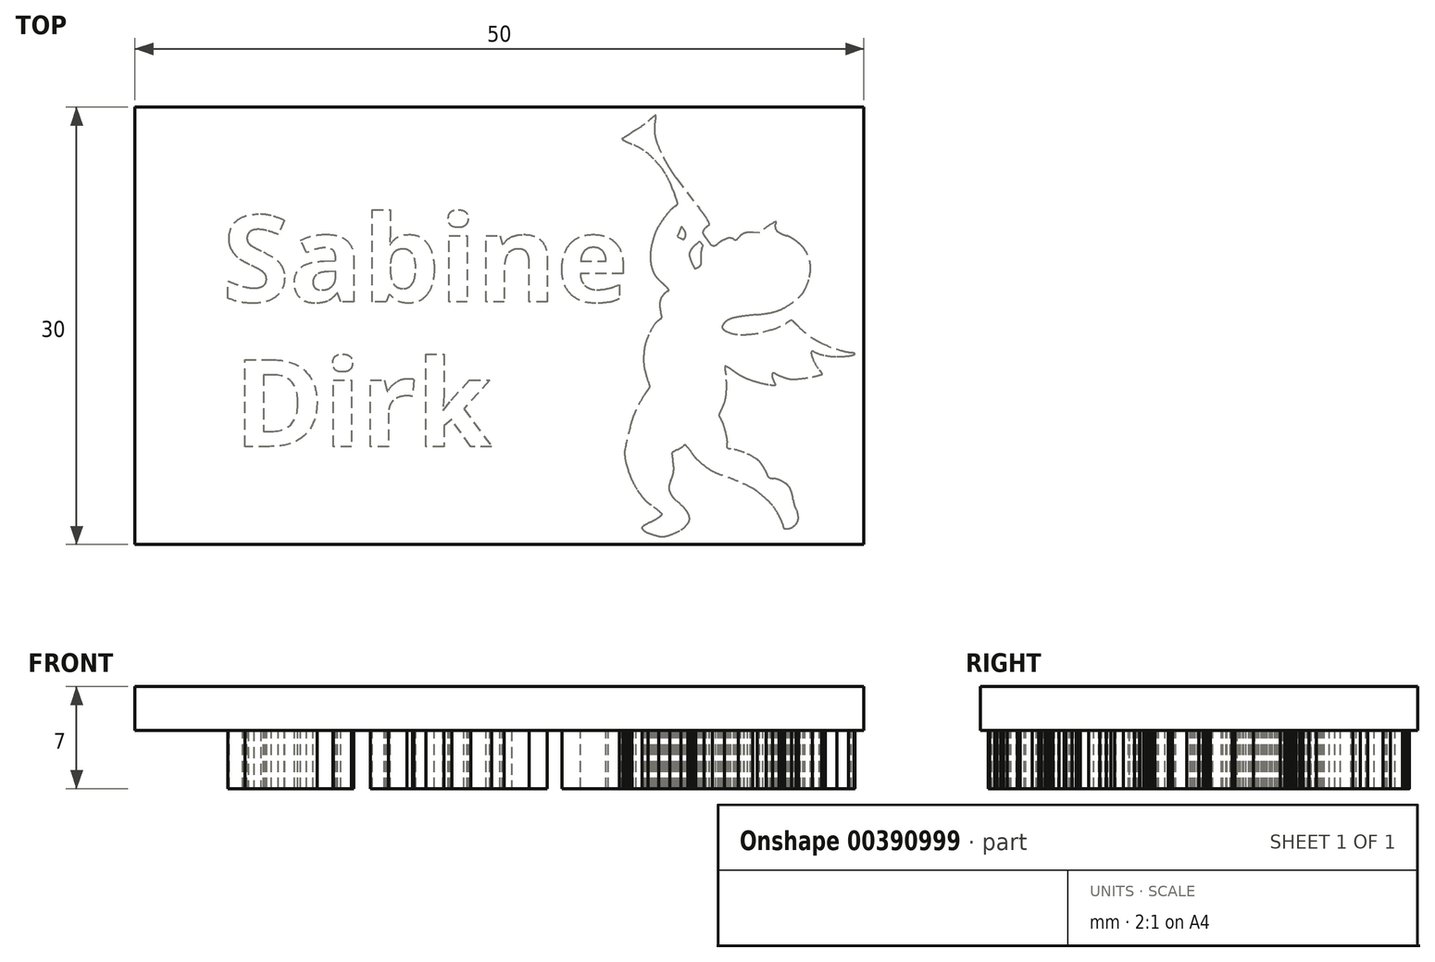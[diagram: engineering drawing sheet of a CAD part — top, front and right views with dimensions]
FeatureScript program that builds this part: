
annotation { "Feature Type Name" : "Feature", "Feature Type Description" : "" }
export const myFeature = defineFeature(function(context is Context, id is Id, definition is map)
    precondition{}
    {
        {
            var Q0;
            Q0=qCreatedBy(makeId("Top.planeOp"),FACE);
            var sketch = newSketch(context, id + "F0", { "sketchPlane" : qUnion([Q0])});
            skLineSegment(sketch, "E0.bottom", {"start": v(25, 15) * mm, "end": v(-25, 15) * mm});
            skLineSegment(sketch, "E0.top", {"start": v(25, -15) * mm, "end": v(-25, -15) * mm});
            skLineSegment(sketch, "E0.left", {"start": v(25, 15) * mm, "end": v(25, -15) * mm});
            skLineSegment(sketch, "E0.right", {"start": v(-25, 15) * mm, "end": v(-25, -15) * mm});
            skPoint(sketch, "E0.middle", {"position": v(0, 0) * mm});
            skSolve(sketch);
        }
        {
            var Q0;
            Q0=makeQuery(id+"F0.imprint","IMPRINT",FACE,{"disambiguationData":[TD([[makeQuery(id+"F0.imprint","IMPRINT",EDGE,{"derivedFrom":sQuery(id+"F0.wireOp",EDGE,"E0.bottom")}),1.0]])]});
            extrude(context, id + "F1", {"entities" : qUnion([Q0]), "depth" : 3 * mm});
        }
        {
            var Q0;
            Q0=makeQuery(id+"F1.opExtrude","CAP_FACE",FACE,{"disambiguationData":[OSD([sQuery(id+"F0.wireOp",EDGE,"E0.bottom"),sQuery(id+"F0.wireOp",EDGE,"E0.top"),sQuery(id+"F0.wireOp",EDGE,"E0.left"),sQuery(id+"F0.wireOp",EDGE,"E0.right")])],"isStart":false});
            var sketch = newSketch(context, id + "F2", { "sketchPlane" : qUnion([Q0])});
            skArc(sketch, "E1", {"start": v(22.16, -3.3) * mm, "mid": v(22.13, -3.26) * mm, "end": v(22.1, -3.21) * mm});
            skArc(sketch, "E2", {"start": v(22.1, -3.21) * mm, "mid": v(22.03, -3.12) * mm, "end": v(21.96, -3.04) * mm});
            skArc(sketch, "E3", {"start": v(21.5, -2.28) * mm, "mid": v(21.7, -2.67) * mm, "end": v(21.96, -3.04) * mm});
            skArc(sketch, "E4", {"start": v(21.43, -2.07) * mm, "mid": v(21.46, -2.18) * mm, "end": v(21.5, -2.28) * mm});
            skArc(sketch, "E5", {"start": v(21.39, -1.87) * mm, "mid": v(21.4, -1.97) * mm, "end": v(21.43, -2.07) * mm});
            skArc(sketch, "E6", {"start": v(21.41, -1.76) * mm, "mid": v(21.4, -1.81) * mm, "end": v(21.39, -1.87) * mm});
            skArc(sketch, "E7", {"start": v(21.46, -1.74) * mm, "mid": v(21.43, -1.75) * mm, "end": v(21.41, -1.76) * mm});
            skArc(sketch, "E8", {"start": v(21.56, -1.77) * mm, "mid": v(21.51, -1.75) * mm, "end": v(21.46, -1.74) * mm});
            skArc(sketch, "E9", {"start": v(21.56, -1.77) * mm, "mid": v(21.95, -1.93) * mm, "end": v(22.36, -2.03) * mm});
            skArc(sketch, "E10", {"start": v(22.36, -2.03) * mm, "mid": v(22.76, -2.1) * mm, "end": v(23.16, -2.12) * mm});
            skArc(sketch, "E11", {"start": v(23.16, -2.12) * mm, "mid": v(23.56, -2.1) * mm, "end": v(23.95, -2.06) * mm});
            skArc(sketch, "E12", {"start": v(23.95, -2.06) * mm, "mid": v(24.14, -2.03) * mm, "end": v(24.32, -1.98) * mm});
            skArc(sketch, "E13", {"start": v(24.32, -1.98) * mm, "mid": v(24.34, -1.97) * mm, "end": v(24.36, -1.96) * mm});
            skArc(sketch, "E14", {"start": v(24.36, -1.96) * mm, "mid": v(24.38, -1.94) * mm, "end": v(24.39, -1.92) * mm});
            skArc(sketch, "E15", {"start": v(24.39, -1.92) * mm, "mid": v(24.36, -1.89) * mm, "end": v(24.31, -1.87) * mm});
            skArc(sketch, "E16", {"start": v(24.31, -1.87) * mm, "mid": v(24.22, -1.85) * mm, "end": v(24.13, -1.84) * mm});
            skArc(sketch, "E17", {"start": v(23.4, -1.68) * mm, "mid": v(23.77, -1.77) * mm, "end": v(24.13, -1.84) * mm});
            skArc(sketch, "E18", {"start": v(22.07, -1.17) * mm, "mid": v(22.72, -1.46) * mm, "end": v(23.4, -1.68) * mm});
            skArc(sketch, "E19", {"start": v(21.48, -0.85) * mm, "mid": v(21.77, -1.02) * mm, "end": v(22.07, -1.17) * mm});
            skArc(sketch, "E20", {"start": v(20.48, -0.01) * mm, "mid": v(20.95, -0.46) * mm, "end": v(21.48, -0.85) * mm});
            skArc(sketch, "E21", {"start": v(20.48, -0.01) * mm, "mid": v(20.37, 0.1) * mm, "end": v(20.26, 0.2) * mm});
            skArc(sketch, "E22", {"start": v(20.26, 0.2) * mm, "mid": v(20.2, 0.25) * mm, "end": v(20.15, 0.3) * mm});
            skLineSegment(sketch, "E23", {"start": v(20.15, 0.3) * mm, "end": v(20.1, 0.35) * mm});
            skArc(sketch, "E24", {"start": v(20.1, 0.35) * mm, "mid": v(20.08, 0.36) * mm, "end": v(20.06, 0.37) * mm});
            skArc(sketch, "E25", {"start": v(20.06, 0.37) * mm, "mid": v(20.05, 0.38) * mm, "end": v(20.03, 0.38) * mm});
            skArc(sketch, "E26", {"start": v(20.03, 0.38) * mm, "mid": v(19.96, 0.35) * mm, "end": v(19.9, 0.31) * mm});
            skArc(sketch, "E27", {"start": v(19.9, 0.31) * mm, "mid": v(19.77, 0.24) * mm, "end": v(19.65, 0.16) * mm});
            skArc(sketch, "E28", {"start": v(18.59, -0.3) * mm, "mid": v(19.13, -0.1) * mm, "end": v(19.65, 0.16) * mm});
            skLineSegment(sketch, "E29", {"start": v(18.59, -0.3) * mm, "end": v(18.07, -0.45) * mm});
            skArc(sketch, "E30", {"start": v(17.03, -0.6) * mm, "mid": v(17.55, -0.54) * mm, "end": v(18.07, -0.45) * mm});
            skArc(sketch, "E31", {"start": v(16.54, -0.6) * mm, "mid": v(16.78, -0.6) * mm, "end": v(17.03, -0.6) * mm});
            skArc(sketch, "E32", {"start": v(15.61, -0.4) * mm, "mid": v(16.06, -0.55) * mm, "end": v(16.54, -0.6) * mm});
            skArc(sketch, "E33", {"start": v(15.42, -0.28) * mm, "mid": v(15.51, -0.34) * mm, "end": v(15.61, -0.4) * mm});
            skArc(sketch, "E34", {"start": v(15.29, -0.11) * mm, "mid": v(15.34, -0.21) * mm, "end": v(15.42, -0.28) * mm});
            skArc(sketch, "E35", {"start": v(15.3, 0) * mm, "mid": v(15.28, -0.06) * mm, "end": v(15.29, -0.11) * mm});
            skArc(sketch, "E36", {"start": v(15.41, 0.17) * mm, "mid": v(15.35, 0.09) * mm, "end": v(15.3, 0) * mm});
            skArc(sketch, "E37", {"start": v(15.75, 0.43) * mm, "mid": v(15.57, 0.32) * mm, "end": v(15.41, 0.17) * mm});
            skArc(sketch, "E38", {"start": v(16.13, 0.56) * mm, "mid": v(15.94, 0.5) * mm, "end": v(15.75, 0.43) * mm});
            skArc(sketch, "E39", {"start": v(16.92, 0.68) * mm, "mid": v(16.52, 0.63) * mm, "end": v(16.13, 0.56) * mm});
            skArc(sketch, "E40", {"start": v(17.66, 0.76) * mm, "mid": v(17.29, 0.72) * mm, "end": v(16.92, 0.68) * mm});
            skArc(sketch, "E41", {"start": v(17.66, 0.76) * mm, "mid": v(18, 0.8) * mm, "end": v(18.35, 0.85) * mm});
            skArc(sketch, "E42", {"start": v(18.35, 0.85) * mm, "mid": v(18.67, 0.91) * mm, "end": v(18.99, 1) * mm});
            skArc(sketch, "E43", {"start": v(18.99, 1) * mm, "mid": v(19.27, 1.1) * mm, "end": v(19.55, 1.24) * mm});
            skArc(sketch, "E44", {"start": v(19.55, 1.24) * mm, "mid": v(20.04, 1.54) * mm, "end": v(20.49, 1.9) * mm});
            skArc(sketch, "E45", {"start": v(20.49, 1.9) * mm, "mid": v(20.67, 2.07) * mm, "end": v(20.83, 2.27) * mm});
            skArc(sketch, "E46", {"start": v(20.83, 2.27) * mm, "mid": v(20.9, 2.36) * mm, "end": v(20.95, 2.47) * mm});
            skArc(sketch, "E47", {"start": v(20.95, 2.47) * mm, "mid": v(21.13, 2.89) * mm, "end": v(21.26, 3.32) * mm});
            skArc(sketch, "E48", {"start": v(21.26, 3.32) * mm, "mid": v(21.3, 3.52) * mm, "end": v(21.34, 3.72) * mm});
            skArc(sketch, "E49", {"start": v(21.34, 3.72) * mm, "mid": v(21.29, 4.46) * mm, "end": v(21, 5.15) * mm});
            skArc(sketch, "E50", {"start": v(21, 5.15) * mm, "mid": v(20.83, 5.38) * mm, "end": v(20.64, 5.58) * mm});
            skArc(sketch, "E51", {"start": v(20.64, 5.58) * mm, "mid": v(20.45, 5.74) * mm, "end": v(20.26, 5.89) * mm});
            skArc(sketch, "E52", {"start": v(20.26, 5.89) * mm, "mid": v(20.08, 6) * mm, "end": v(19.89, 6.11) * mm});
            skArc(sketch, "E53", {"start": v(19.89, 6.11) * mm, "mid": v(19.8, 6.15) * mm, "end": v(19.71, 6.18) * mm});
            skArc(sketch, "E54", {"start": v(19.38, 6.3) * mm, "mid": v(19.55, 6.24) * mm, "end": v(19.71, 6.18) * mm});
            skArc(sketch, "E55", {"start": v(19.11, 6.45) * mm, "mid": v(19.25, 6.37) * mm, "end": v(19.38, 6.3) * mm});
            skArc(sketch, "E56", {"start": v(18.95, 6.66) * mm, "mid": v(19.01, 6.54) * mm, "end": v(19.11, 6.45) * mm});
            skArc(sketch, "E57", {"start": v(18.91, 6.9) * mm, "mid": v(18.92, 6.77) * mm, "end": v(18.95, 6.66) * mm});
            skArc(sketch, "E58", {"start": v(18.94, 6.99) * mm, "mid": v(18.92, 6.94) * mm, "end": v(18.91, 6.9) * mm});
            skArc(sketch, "E59", {"start": v(18.98, 7.02) * mm, "mid": v(18.96, 7) * mm, "end": v(18.94, 6.99) * mm});
            skArc(sketch, "E60", {"start": v(18.98, 7.02) * mm, "mid": v(19, 7.06) * mm, "end": v(19, 7.1) * mm});
            skArc(sketch, "E61", {"start": v(19, 7.1) * mm, "mid": v(18.96, 7.13) * mm, "end": v(18.92, 7.12) * mm});
            skArc(sketch, "E62", {"start": v(18.92, 7.12) * mm, "mid": v(18.84, 7.1) * mm, "end": v(18.77, 7.05) * mm});
            skArc(sketch, "E63", {"start": v(18.77, 7.05) * mm, "mid": v(18.28, 6.74) * mm, "end": v(17.84, 6.36) * mm});
            skLineSegment(sketch, "E64", {"start": v(17.84, 6.36) * mm, "end": v(17.4, 6.4) * mm});
            skArc(sketch, "E65", {"start": v(17.4, 6.4) * mm, "mid": v(17.31, 6.4) * mm, "end": v(17.22, 6.4) * mm});
            skArc(sketch, "E66", {"start": v(17.22, 6.4) * mm, "mid": v(17, 6.4) * mm, "end": v(16.77, 6.34) * mm});
            skArc(sketch, "E67", {"start": v(16.77, 6.34) * mm, "mid": v(16.6, 6.23) * mm, "end": v(16.45, 6.1) * mm});
            skArc(sketch, "E68", {"start": v(16.34, 5.97) * mm, "mid": v(16.4, 6.03) * mm, "end": v(16.45, 6.1) * mm});
            skArc(sketch, "E69", {"start": v(16.21, 5.9) * mm, "mid": v(16.28, 5.92) * mm, "end": v(16.34, 5.97) * mm});
            skArc(sketch, "E70", {"start": v(16.06, 5.95) * mm, "mid": v(16.13, 5.92) * mm, "end": v(16.21, 5.9) * mm});
            skArc(sketch, "E71", {"start": v(16.06, 5.95) * mm, "mid": v(15.93, 6) * mm, "end": v(15.8, 6.03) * mm});
            skArc(sketch, "E72", {"start": v(15.8, 6.03) * mm, "mid": v(15.71, 6.01) * mm, "end": v(15.63, 5.99) * mm});
            skArc(sketch, "E73", {"start": v(15.63, 5.99) * mm, "mid": v(15.46, 5.92) * mm, "end": v(15.29, 5.84) * mm});
            skArc(sketch, "E74", {"start": v(15.29, 5.84) * mm, "mid": v(15.14, 5.75) * mm, "end": v(15, 5.66) * mm});
            skArc(sketch, "E75", {"start": v(14.82, 5.53) * mm, "mid": v(14.92, 5.58) * mm, "end": v(15, 5.66) * mm});
            skArc(sketch, "E76", {"start": v(14.57, 5.52) * mm, "mid": v(14.7, 5.5) * mm, "end": v(14.82, 5.53) * mm});
            skArc(sketch, "E77", {"start": v(14.38, 5.74) * mm, "mid": v(14.46, 5.62) * mm, "end": v(14.57, 5.52) * mm});
            skArc(sketch, "E78", {"start": v(14.38, 5.74) * mm, "mid": v(14.26, 5.92) * mm, "end": v(14.13, 6.1) * mm});
            skArc(sketch, "E79", {"start": v(14, 6.28) * mm, "mid": v(14.05, 6.18) * mm, "end": v(14.13, 6.1) * mm});
            skArc(sketch, "E80", {"start": v(13.98, 6.52) * mm, "mid": v(13.96, 6.4) * mm, "end": v(14, 6.28) * mm});
            skArc(sketch, "E81", {"start": v(14.2, 6.78) * mm, "mid": v(14.07, 6.66) * mm, "end": v(13.98, 6.52) * mm});
            skLineSegment(sketch, "E82", {"start": v(14.2, 6.78) * mm, "end": v(14.42, 6.98) * mm});
            skArc(sketch, "E83", {"start": v(14.42, 6.98) * mm, "mid": v(14.27, 7.27) * mm, "end": v(14.1, 7.55) * mm});
            skArc(sketch, "E84", {"start": v(14.1, 7.55) * mm, "mid": v(13.9, 7.8) * mm, "end": v(13.71, 8.06) * mm});
            skArc(sketch, "E85", {"start": v(12.17, 10.08) * mm, "mid": v(12.93, 9.06) * mm, "end": v(13.71, 8.06) * mm});
            skArc(sketch, "E86", {"start": v(11.83, 10.56) * mm, "mid": v(12, 10.32) * mm, "end": v(12.17, 10.08) * mm});
            skArc(sketch, "E87", {"start": v(11.52, 11.06) * mm, "mid": v(11.67, 10.8) * mm, "end": v(11.83, 10.56) * mm});
            skArc(sketch, "E88", {"start": v(11.52, 11.06) * mm, "mid": v(11.4, 11.32) * mm, "end": v(11.26, 11.57) * mm});
            skArc(sketch, "E89", {"start": v(10.8, 12.6) * mm, "mid": v(11, 12.08) * mm, "end": v(11.26, 11.57) * mm});
            skArc(sketch, "E90", {"start": v(10.66, 13.14) * mm, "mid": v(10.71, 12.87) * mm, "end": v(10.8, 12.6) * mm});
            skArc(sketch, "E91", {"start": v(10.64, 13.68) * mm, "mid": v(10.64, 13.4) * mm, "end": v(10.66, 13.14) * mm});
            skArc(sketch, "E92", {"start": v(10.66, 13.94) * mm, "mid": v(10.65, 13.81) * mm, "end": v(10.64, 13.68) * mm});
            skArc(sketch, "E93", {"start": v(10.69, 14.07) * mm, "mid": v(10.67, 14) * mm, "end": v(10.66, 13.94) * mm});
            skLineSegment(sketch, "E94", {"start": v(10.69, 14.07) * mm, "end": v(10.73, 14.2) * mm});
            skArc(sketch, "E95", {"start": v(10.73, 14.2) * mm, "mid": v(10.74, 14.26) * mm, "end": v(10.75, 14.33) * mm});
            skArc(sketch, "E96", {"start": v(10.75, 14.33) * mm, "mid": v(10.75, 14.36) * mm, "end": v(10.75, 14.4) * mm});
            skArc(sketch, "E97", {"start": v(10.75, 14.4) * mm, "mid": v(10.74, 14.42) * mm, "end": v(10.7, 14.43) * mm});
            skArc(sketch, "E98", {"start": v(10.7, 14.43) * mm, "mid": v(10.65, 14.4) * mm, "end": v(10.6, 14.37) * mm});
            skArc(sketch, "E99", {"start": v(10.6, 14.37) * mm, "mid": v(10.4, 14.2) * mm, "end": v(10.2, 14.04) * mm});
            skArc(sketch, "E100", {"start": v(9.37, 13.45) * mm, "mid": v(9.8, 13.73) * mm, "end": v(10.2, 14.04) * mm});
            skArc(sketch, "E101", {"start": v(9.37, 13.45) * mm, "mid": v(9.16, 13.31) * mm, "end": v(8.96, 13.18) * mm});
            skArc(sketch, "E102", {"start": v(8.54, 12.92) * mm, "mid": v(8.75, 13.04) * mm, "end": v(8.96, 13.18) * mm});
            skArc(sketch, "E103", {"start": v(8.44, 12.86) * mm, "mid": v(8.5, 12.89) * mm, "end": v(8.54, 12.92) * mm});
            skArc(sketch, "E104", {"start": v(8.44, 12.86) * mm, "mid": v(8.42, 12.85) * mm, "end": v(8.41, 12.82) * mm});
            skArc(sketch, "E105", {"start": v(8.41, 12.82) * mm, "mid": v(8.43, 12.8) * mm, "end": v(8.45, 12.77) * mm});
            skArc(sketch, "E106", {"start": v(8.45, 12.77) * mm, "mid": v(8.55, 12.71) * mm, "end": v(8.66, 12.66) * mm});
            skArc(sketch, "E107", {"start": v(8.66, 12.66) * mm, "mid": v(8.87, 12.56) * mm, "end": v(9.09, 12.46) * mm});
            skArc(sketch, "E108", {"start": v(9.9, 12.03) * mm, "mid": v(9.5, 12.26) * mm, "end": v(9.09, 12.46) * mm});
            skArc(sketch, "E109", {"start": v(10.58, 11.44) * mm, "mid": v(10.26, 11.75) * mm, "end": v(9.9, 12.03) * mm});
            skArc(sketch, "E110", {"start": v(11.15, 10.78) * mm, "mid": v(10.88, 11.12) * mm, "end": v(10.58, 11.44) * mm});
            skArc(sketch, "E111", {"start": v(11.39, 10.43) * mm, "mid": v(11.28, 10.61) * mm, "end": v(11.15, 10.78) * mm});
            skArc(sketch, "E112", {"start": v(11.77, 9.7) * mm, "mid": v(11.59, 10.07) * mm, "end": v(11.39, 10.43) * mm});
            skArc(sketch, "E113", {"start": v(11.9, 9.32) * mm, "mid": v(11.84, 9.5) * mm, "end": v(11.77, 9.7) * mm});
            skArc(sketch, "E114", {"start": v(11.9, 9.32) * mm, "mid": v(11.97, 9.13) * mm, "end": v(12.05, 8.95) * mm});
            skArc(sketch, "E115", {"start": v(12.19, 8.58) * mm, "mid": v(12.12, 8.77) * mm, "end": v(12.05, 8.95) * mm});
            skArc(sketch, "E116", {"start": v(12.21, 8.5) * mm, "mid": v(12.2, 8.54) * mm, "end": v(12.19, 8.58) * mm});
            skArc(sketch, "E117", {"start": v(12.23, 8.4) * mm, "mid": v(12.23, 8.44) * mm, "end": v(12.21, 8.5) * mm});
            skArc(sketch, "E118", {"start": v(12.22, 8.35) * mm, "mid": v(12.23, 8.37) * mm, "end": v(12.23, 8.4) * mm});
            skArc(sketch, "E119", {"start": v(12.08, 8.22) * mm, "mid": v(12.16, 8.28) * mm, "end": v(12.22, 8.35) * mm});
            skArc(sketch, "E120", {"start": v(12.08, 8.22) * mm, "mid": v(11.93, 8.1) * mm, "end": v(11.8, 7.98) * mm});
            skArc(sketch, "E121", {"start": v(11.8, 7.98) * mm, "mid": v(11.54, 7.7) * mm, "end": v(11.31, 7.42) * mm});
            skArc(sketch, "E122", {"start": v(11.31, 7.42) * mm, "mid": v(11.11, 7.12) * mm, "end": v(10.92, 6.82) * mm});
            skArc(sketch, "E123", {"start": v(10.92, 6.82) * mm, "mid": v(10.75, 6.51) * mm, "end": v(10.63, 6.19) * mm});
            skArc(sketch, "E124", {"start": v(10.63, 6.19) * mm, "mid": v(10.53, 5.87) * mm, "end": v(10.44, 5.54) * mm});
            skArc(sketch, "E125", {"start": v(10.44, 5.54) * mm, "mid": v(10.39, 5.22) * mm, "end": v(10.36, 4.9) * mm});
            skArc(sketch, "E126", {"start": v(10.36, 4.9) * mm, "mid": v(10.36, 4.58) * mm, "end": v(10.4, 4.26) * mm});
            skArc(sketch, "E127", {"start": v(10.4, 4.26) * mm, "mid": v(10.46, 3.96) * mm, "end": v(10.57, 3.68) * mm});
            skArc(sketch, "E128", {"start": v(10.57, 3.68) * mm, "mid": v(10.63, 3.54) * mm, "end": v(10.71, 3.42) * mm});
            skArc(sketch, "E129", {"start": v(10.71, 3.42) * mm, "mid": v(10.9, 3.2) * mm, "end": v(11.1, 3) * mm});
            skArc(sketch, "E130", {"start": v(11.52, 2.6) * mm, "mid": v(11.32, 2.8) * mm, "end": v(11.1, 3) * mm});
            skArc(sketch, "E131", {"start": v(11.6, 2.5) * mm, "mid": v(11.57, 2.55) * mm, "end": v(11.52, 2.6) * mm});
            skArc(sketch, "E132", {"start": v(11.57, 2.38) * mm, "mid": v(11.62, 2.43) * mm, "end": v(11.6, 2.5) * mm});
            skArc(sketch, "E133", {"start": v(11.57, 2.38) * mm, "mid": v(11.5, 2.36) * mm, "end": v(11.45, 2.32) * mm});
            skArc(sketch, "E134", {"start": v(11.45, 2.32) * mm, "mid": v(11.26, 2.14) * mm, "end": v(11.1, 1.92) * mm});
            skArc(sketch, "E135", {"start": v(11.1, 1.92) * mm, "mid": v(11.02, 1.68) * mm, "end": v(11, 1.42) * mm});
            skArc(sketch, "E136", {"start": v(11, 1.42) * mm, "mid": v(11.02, 1.17) * mm, "end": v(11.07, 0.92) * mm});
            skArc(sketch, "E137", {"start": v(11.14, 0.69) * mm, "mid": v(11.1, 0.8) * mm, "end": v(11.07, 0.92) * mm});
            skArc(sketch, "E138", {"start": v(11.15, 0.57) * mm, "mid": v(11.15, 0.63) * mm, "end": v(11.14, 0.69) * mm});
            skArc(sketch, "E139", {"start": v(11.07, 0.48) * mm, "mid": v(11.11, 0.52) * mm, "end": v(11.15, 0.57) * mm});
            skArc(sketch, "E140", {"start": v(11.07, 0.48) * mm, "mid": v(10.98, 0.4) * mm, "end": v(10.88, 0.34) * mm});
            skArc(sketch, "E141", {"start": v(10.88, 0.34) * mm, "mid": v(10.79, 0.27) * mm, "end": v(10.7, 0.18) * mm});
            skArc(sketch, "E142", {"start": v(10.7, 0.18) * mm, "mid": v(10.46, -0.2) * mm, "end": v(10.25, -0.6) * mm});
            skArc(sketch, "E143", {"start": v(10.25, -0.6) * mm, "mid": v(10.13, -0.9) * mm, "end": v(10.02, -1.2) * mm});
            skArc(sketch, "E144", {"start": v(10.02, -1.2) * mm, "mid": v(9.97, -1.4) * mm, "end": v(9.94, -1.6) * mm});
            skArc(sketch, "E145", {"start": v(9.94, -1.6) * mm, "mid": v(9.9, -2) * mm, "end": v(9.9, -2.4) * mm});
            skArc(sketch, "E146", {"start": v(9.9, -2.4) * mm, "mid": v(9.92, -2.76) * mm, "end": v(10, -3.13) * mm});
            skArc(sketch, "E147", {"start": v(10, -3.13) * mm, "mid": v(10.08, -3.46) * mm, "end": v(10.19, -3.8) * mm});
            skLineSegment(sketch, "E148", {"start": v(10.19, -3.8) * mm, "end": v(10.3, -4.1) * mm});
            skArc(sketch, "E149", {"start": v(10.3, -4.25) * mm, "mid": v(10.32, -4.18) * mm, "end": v(10.3, -4.1) * mm});
            skArc(sketch, "E150", {"start": v(10.11, -4.5) * mm, "mid": v(10.21, -4.38) * mm, "end": v(10.3, -4.25) * mm});
            skArc(sketch, "E151", {"start": v(10.11, -4.5) * mm, "mid": v(10.02, -4.62) * mm, "end": v(9.94, -4.75) * mm});
            skArc(sketch, "E152", {"start": v(9.94, -4.75) * mm, "mid": v(9.64, -5.25) * mm, "end": v(9.38, -5.77) * mm});
            skArc(sketch, "E153", {"start": v(9.38, -5.77) * mm, "mid": v(9.27, -6) * mm, "end": v(9.17, -6.24) * mm});
            skArc(sketch, "E154", {"start": v(9.17, -6.24) * mm, "mid": v(9.1, -6.47) * mm, "end": v(9.03, -6.7) * mm});
            skArc(sketch, "E155", {"start": v(9.03, -6.7) * mm, "mid": v(8.81, -7.57) * mm, "end": v(8.61, -8.45) * mm});
            skArc(sketch, "E156", {"start": v(8.61, -8.45) * mm, "mid": v(8.6, -8.61) * mm, "end": v(8.6, -8.78) * mm});
            skArc(sketch, "E157", {"start": v(8.6, -8.78) * mm, "mid": v(8.62, -9.1) * mm, "end": v(8.68, -9.4) * mm});
            skArc(sketch, "E158", {"start": v(8.68, -9.4) * mm, "mid": v(8.72, -9.54) * mm, "end": v(8.76, -9.67) * mm});
            skArc(sketch, "E159", {"start": v(8.76, -9.67) * mm, "mid": v(8.8, -9.8) * mm, "end": v(8.85, -9.91) * mm});
            skArc(sketch, "E160", {"start": v(8.93, -10.15) * mm, "mid": v(8.9, -10.03) * mm, "end": v(8.85, -9.91) * mm});
            skArc(sketch, "E161", {"start": v(8.93, -10.15) * mm, "mid": v(9, -10.36) * mm, "end": v(9.09, -10.57) * mm});
            skArc(sketch, "E162", {"start": v(9.09, -10.57) * mm, "mid": v(9.27, -10.93) * mm, "end": v(9.47, -11.27) * mm});
            skArc(sketch, "E163", {"start": v(9.47, -11.27) * mm, "mid": v(9.64, -11.52) * mm, "end": v(9.82, -11.76) * mm});
            skArc(sketch, "E164", {"start": v(9.82, -11.76) * mm, "mid": v(9.96, -11.92) * mm, "end": v(10.13, -12.08) * mm});
            skArc(sketch, "E165", {"start": v(10.13, -12.08) * mm, "mid": v(10.26, -12.18) * mm, "end": v(10.4, -12.28) * mm});
            skArc(sketch, "E166", {"start": v(11.18, -12.91) * mm, "mid": v(10.8, -12.59) * mm, "end": v(10.4, -12.28) * mm});
            skArc(sketch, "E167", {"start": v(11.01, -13.08) * mm, "mid": v(11.1, -13) * mm, "end": v(11.18, -12.91) * mm});
            skArc(sketch, "E168", {"start": v(10.63, -13.32) * mm, "mid": v(10.83, -13.21) * mm, "end": v(11.01, -13.08) * mm});
            skArc(sketch, "E169", {"start": v(10.29, -13.5) * mm, "mid": v(10.46, -13.41) * mm, "end": v(10.63, -13.32) * mm});
            skArc(sketch, "E170", {"start": v(10.29, -13.5) * mm, "mid": v(10.13, -13.58) * mm, "end": v(9.98, -13.67) * mm});
            skArc(sketch, "E171", {"start": v(9.98, -13.67) * mm, "mid": v(9.92, -13.7) * mm, "end": v(9.86, -13.75) * mm});
            skArc(sketch, "E172", {"start": v(9.86, -13.75) * mm, "mid": v(9.8, -13.8) * mm, "end": v(9.77, -13.86) * mm});
            skArc(sketch, "E173", {"start": v(9.77, -13.86) * mm, "mid": v(9.78, -13.9) * mm, "end": v(9.8, -13.92) * mm});
            skArc(sketch, "E174", {"start": v(9.8, -13.92) * mm, "mid": v(9.97, -14.1) * mm, "end": v(10.2, -14.21) * mm});
            skArc(sketch, "E175", {"start": v(10.2, -14.21) * mm, "mid": v(10.56, -14.33) * mm, "end": v(10.93, -14.43) * mm});
            skArc(sketch, "E176", {"start": v(10.93, -14.43) * mm, "mid": v(11.12, -14.46) * mm, "end": v(11.32, -14.45) * mm});
            skArc(sketch, "E177", {"start": v(11.32, -14.45) * mm, "mid": v(11.5, -14.41) * mm, "end": v(11.69, -14.35) * mm});
            skArc(sketch, "E178", {"start": v(11.69, -14.35) * mm, "mid": v(12.07, -14.2) * mm, "end": v(12.44, -14.01) * mm});
            skArc(sketch, "E179", {"start": v(12.44, -14.01) * mm, "mid": v(12.7, -13.82) * mm, "end": v(12.92, -13.58) * mm});
            skArc(sketch, "E180", {"start": v(12.92, -13.58) * mm, "mid": v(13, -13.43) * mm, "end": v(13.05, -13.26) * mm});
            skArc(sketch, "E181", {"start": v(13.05, -13.26) * mm, "mid": v(13.04, -13.12) * mm, "end": v(13, -13) * mm});
            skArc(sketch, "E182", {"start": v(13, -13) * mm, "mid": v(12.88, -12.75) * mm, "end": v(12.7, -12.54) * mm});
            skArc(sketch, "E183", {"start": v(12.7, -12.54) * mm, "mid": v(12.43, -12.25) * mm, "end": v(12.12, -11.99) * mm});
            skArc(sketch, "E184", {"start": v(11.8, -11.6) * mm, "mid": v(11.94, -11.8) * mm, "end": v(12.12, -11.99) * mm});
            skArc(sketch, "E185", {"start": v(11.62, -11.16) * mm, "mid": v(11.69, -11.4) * mm, "end": v(11.8, -11.6) * mm});
            skArc(sketch, "E186", {"start": v(11.64, -10.95) * mm, "mid": v(11.62, -11.05) * mm, "end": v(11.62, -11.16) * mm});
            skArc(sketch, "E187", {"start": v(11.76, -10.62) * mm, "mid": v(11.7, -10.78) * mm, "end": v(11.64, -10.95) * mm});
            skArc(sketch, "E188", {"start": v(11.76, -10.62) * mm, "mid": v(11.83, -10.44) * mm, "end": v(11.9, -10.27) * mm});
            skArc(sketch, "E189", {"start": v(11.9, -10.27) * mm, "mid": v(11.93, -10.15) * mm, "end": v(11.95, -10.04) * mm});
            skArc(sketch, "E190", {"start": v(11.95, -10.04) * mm, "mid": v(11.97, -9.86) * mm, "end": v(11.96, -9.69) * mm});
            skArc(sketch, "E191", {"start": v(11.96, -9.69) * mm, "mid": v(11.94, -9.47) * mm, "end": v(11.9, -9.25) * mm});
            skArc(sketch, "E192", {"start": v(11.84, -8.9) * mm, "mid": v(11.87, -9.07) * mm, "end": v(11.9, -9.25) * mm});
            skArc(sketch, "E193", {"start": v(11.84, -8.71) * mm, "mid": v(11.83, -8.8) * mm, "end": v(11.84, -8.9) * mm});
            skArc(sketch, "E194", {"start": v(11.96, -8.63) * mm, "mid": v(11.9, -8.67) * mm, "end": v(11.84, -8.71) * mm});
            skArc(sketch, "E195", {"start": v(12.2, -8.5) * mm, "mid": v(12.08, -8.56) * mm, "end": v(11.96, -8.63) * mm});
            skArc(sketch, "E196", {"start": v(12.2, -8.5) * mm, "mid": v(12.33, -8.43) * mm, "end": v(12.46, -8.36) * mm});
            skArc(sketch, "E197", {"start": v(12.46, -8.36) * mm, "mid": v(12.53, -8.3) * mm, "end": v(12.6, -8.25) * mm});
            skArc(sketch, "E198", {"start": v(12.73, -8.17) * mm, "mid": v(12.66, -8.2) * mm, "end": v(12.6, -8.25) * mm});
            skArc(sketch, "E199", {"start": v(12.82, -8.23) * mm, "mid": v(12.78, -8.2) * mm, "end": v(12.73, -8.17) * mm});
            skArc(sketch, "E200", {"start": v(13.26, -8.81) * mm, "mid": v(13.06, -8.5) * mm, "end": v(12.82, -8.23) * mm});
            skArc(sketch, "E201", {"start": v(13.26, -8.81) * mm, "mid": v(13.36, -8.95) * mm, "end": v(13.48, -9.07) * mm});
            skArc(sketch, "E202", {"start": v(13.48, -9.07) * mm, "mid": v(13.75, -9.33) * mm, "end": v(14.04, -9.58) * mm});
            skArc(sketch, "E203", {"start": v(14.04, -9.58) * mm, "mid": v(14.32, -9.78) * mm, "end": v(14.6, -9.97) * mm});
            skArc(sketch, "E204", {"start": v(14.6, -9.97) * mm, "mid": v(15.01, -10.14) * mm, "end": v(15.43, -10.3) * mm});
            skArc(sketch, "E205", {"start": v(16.38, -10.68) * mm, "mid": v(15.9, -10.48) * mm, "end": v(15.43, -10.3) * mm});
            skArc(sketch, "E206", {"start": v(17.38, -11.16) * mm, "mid": v(16.89, -10.91) * mm, "end": v(16.38, -10.68) * mm});
            skArc(sketch, "E207", {"start": v(17.7, -11.37) * mm, "mid": v(17.54, -11.26) * mm, "end": v(17.38, -11.16) * mm});
            skArc(sketch, "E208", {"start": v(18.3, -11.88) * mm, "mid": v(18, -11.62) * mm, "end": v(17.7, -11.37) * mm});
            skArc(sketch, "E209", {"start": v(18.75, -12.34) * mm, "mid": v(18.54, -12.1) * mm, "end": v(18.3, -11.88) * mm});
            skArc(sketch, "E210", {"start": v(19.18, -13.01) * mm, "mid": v(18.97, -12.67) * mm, "end": v(18.75, -12.34) * mm});
            skArc(sketch, "E211", {"start": v(19.41, -13.55) * mm, "mid": v(19.31, -13.28) * mm, "end": v(19.18, -13.01) * mm});
            skArc(sketch, "E212", {"start": v(19.41, -13.55) * mm, "mid": v(19.45, -13.7) * mm, "end": v(19.49, -13.86) * mm});
            skArc(sketch, "E213", {"start": v(19.49, -13.86) * mm, "mid": v(19.52, -13.9) * mm, "end": v(19.56, -13.9) * mm});
            skArc(sketch, "E214", {"start": v(19.56, -13.9) * mm, "mid": v(19.81, -13.91) * mm, "end": v(20.05, -13.85) * mm});
            skArc(sketch, "E215", {"start": v(20.05, -13.85) * mm, "mid": v(20.21, -13.73) * mm, "end": v(20.35, -13.6) * mm});
            skArc(sketch, "E216", {"start": v(20.35, -13.6) * mm, "mid": v(20.42, -13.5) * mm, "end": v(20.48, -13.4) * mm});
            skArc(sketch, "E217", {"start": v(20.48, -13.4) * mm, "mid": v(20.5, -13.3) * mm, "end": v(20.5, -13.18) * mm});
            skArc(sketch, "E218", {"start": v(20.5, -13.18) * mm, "mid": v(20.46, -12.8) * mm, "end": v(20.3, -12.47) * mm});
            skArc(sketch, "E219", {"start": v(20.22, -12.28) * mm, "mid": v(20.25, -12.38) * mm, "end": v(20.3, -12.47) * mm});
            skArc(sketch, "E220", {"start": v(20.16, -11.97) * mm, "mid": v(20.18, -12.12) * mm, "end": v(20.22, -12.28) * mm});
            skArc(sketch, "E221", {"start": v(20.16, -11.97) * mm, "mid": v(20.14, -11.82) * mm, "end": v(20.11, -11.66) * mm});
            skArc(sketch, "E222", {"start": v(20.11, -11.66) * mm, "mid": v(20.09, -11.56) * mm, "end": v(20.06, -11.46) * mm});
            skArc(sketch, "E223", {"start": v(20.06, -11.46) * mm, "mid": v(19.97, -11.21) * mm, "end": v(19.83, -10.99) * mm});
            skArc(sketch, "E224", {"start": v(19.83, -10.99) * mm, "mid": v(19.74, -10.9) * mm, "end": v(19.63, -10.8) * mm});
            skArc(sketch, "E225", {"start": v(19.63, -10.8) * mm, "mid": v(19.42, -10.68) * mm, "end": v(19.2, -10.57) * mm});
            skArc(sketch, "E226", {"start": v(19.2, -10.57) * mm, "mid": v(19, -10.5) * mm, "end": v(18.79, -10.47) * mm});
            skArc(sketch, "E227", {"start": v(18.62, -10.45) * mm, "mid": v(18.7, -10.47) * mm, "end": v(18.79, -10.47) * mm});
            skArc(sketch, "E228", {"start": v(18.43, -10.34) * mm, "mid": v(18.52, -10.4) * mm, "end": v(18.62, -10.45) * mm});
            skArc(sketch, "E229", {"start": v(18.36, -10.18) * mm, "mid": v(18.38, -10.27) * mm, "end": v(18.43, -10.34) * mm});
            skArc(sketch, "E230", {"start": v(18.36, -10.18) * mm, "mid": v(18.33, -10.1) * mm, "end": v(18.3, -10.01) * mm});
            skArc(sketch, "E231", {"start": v(18.3, -10.01) * mm, "mid": v(18.19, -9.8) * mm, "end": v(18.06, -9.6) * mm});
            skArc(sketch, "E232", {"start": v(18.06, -9.6) * mm, "mid": v(17.94, -9.43) * mm, "end": v(17.8, -9.26) * mm});
            skArc(sketch, "E233", {"start": v(17.8, -9.26) * mm, "mid": v(17.73, -9.2) * mm, "end": v(17.65, -9.14) * mm});
            skArc(sketch, "E234", {"start": v(17.65, -9.14) * mm, "mid": v(17.25, -8.9) * mm, "end": v(16.82, -8.7) * mm});
            skArc(sketch, "E235", {"start": v(16.82, -8.7) * mm, "mid": v(16.36, -8.55) * mm, "end": v(15.9, -8.44) * mm});
            skArc(sketch, "E236", {"start": v(15.72, -8.4) * mm, "mid": v(15.8, -8.43) * mm, "end": v(15.9, -8.44) * mm});
            skArc(sketch, "E237", {"start": v(15.63, -8.37) * mm, "mid": v(15.67, -8.39) * mm, "end": v(15.72, -8.4) * mm});
            skArc(sketch, "E238", {"start": v(15.59, -8.28) * mm, "mid": v(15.6, -8.33) * mm, "end": v(15.63, -8.37) * mm});
            skArc(sketch, "E239", {"start": v(15.62, -8.13) * mm, "mid": v(15.6, -8.2) * mm, "end": v(15.59, -8.28) * mm});
            skArc(sketch, "E240", {"start": v(15.62, -8.13) * mm, "mid": v(15.64, -8.03) * mm, "end": v(15.65, -7.93) * mm});
            skArc(sketch, "E241", {"start": v(15.65, -7.93) * mm, "mid": v(15.62, -7.75) * mm, "end": v(15.59, -7.57) * mm});
            skArc(sketch, "E242", {"start": v(15.59, -7.57) * mm, "mid": v(15.5, -7.19) * mm, "end": v(15.39, -6.81) * mm});
            skArc(sketch, "E243", {"start": v(15.39, -6.81) * mm, "mid": v(15.3, -6.58) * mm, "end": v(15.18, -6.37) * mm});
            skArc(sketch, "E244", {"start": v(15.1, -6.24) * mm, "mid": v(15.14, -6.3) * mm, "end": v(15.18, -6.37) * mm});
            skArc(sketch, "E245", {"start": v(15.08, -6.06) * mm, "mid": v(15.07, -6.15) * mm, "end": v(15.1, -6.24) * mm});
            skArc(sketch, "E246", {"start": v(15.2, -5.8) * mm, "mid": v(15.14, -5.92) * mm, "end": v(15.08, -6.06) * mm});
            skArc(sketch, "E247", {"start": v(15.2, -5.8) * mm, "mid": v(15.36, -5.5) * mm, "end": v(15.47, -5.18) * mm});
            skArc(sketch, "E248", {"start": v(15.47, -5.18) * mm, "mid": v(15.54, -4.82) * mm, "end": v(15.58, -4.44) * mm});
            skArc(sketch, "E249", {"start": v(15.58, -4.44) * mm, "mid": v(15.59, -3.91) * mm, "end": v(15.54, -3.38) * mm});
            skArc(sketch, "E250", {"start": v(15.46, -2.85) * mm, "mid": v(15.5, -3.12) * mm, "end": v(15.54, -3.38) * mm});
            skArc(sketch, "E251", {"start": v(15.47, -2.78) * mm, "mid": v(15.46, -2.81) * mm, "end": v(15.46, -2.85) * mm});
            skArc(sketch, "E252", {"start": v(15.52, -2.77) * mm, "mid": v(15.5, -2.77) * mm, "end": v(15.47, -2.78) * mm});
            skArc(sketch, "E253", {"start": v(15.72, -2.88) * mm, "mid": v(15.62, -2.82) * mm, "end": v(15.52, -2.77) * mm});
            skArc(sketch, "E254", {"start": v(16.13, -3.14) * mm, "mid": v(15.93, -3) * mm, "end": v(15.72, -2.88) * mm});
            skArc(sketch, "E255", {"start": v(16.13, -3.14) * mm, "mid": v(16.32, -3.27) * mm, "end": v(16.52, -3.4) * mm});
            skArc(sketch, "E256", {"start": v(16.52, -3.4) * mm, "mid": v(16.77, -3.53) * mm, "end": v(17.02, -3.64) * mm});
            skArc(sketch, "E257", {"start": v(17.02, -3.64) * mm, "mid": v(17.37, -3.76) * mm, "end": v(17.71, -3.86) * mm});
            skArc(sketch, "E258", {"start": v(17.71, -3.86) * mm, "mid": v(18.12, -3.97) * mm, "end": v(18.54, -4.04) * mm});
            skArc(sketch, "E259", {"start": v(18.54, -4.04) * mm, "mid": v(18.69, -4.06) * mm, "end": v(18.84, -4.07) * mm});
            skArc(sketch, "E260", {"start": v(18.84, -4.07) * mm, "mid": v(18.88, -4.07) * mm, "end": v(18.93, -4.06) * mm});
            skArc(sketch, "E261", {"start": v(18.93, -4.06) * mm, "mid": v(18.94, -4.06) * mm, "end": v(18.96, -4.04) * mm});
            skArc(sketch, "E262", {"start": v(18.96, -4.04) * mm, "mid": v(18.9, -3.92) * mm, "end": v(18.83, -3.8) * mm});
            skArc(sketch, "E263", {"start": v(18.71, -3.47) * mm, "mid": v(18.76, -3.64) * mm, "end": v(18.83, -3.8) * mm});
            skArc(sketch, "E264", {"start": v(18.71, -3.33) * mm, "mid": v(18.7, -3.4) * mm, "end": v(18.71, -3.47) * mm});
            skArc(sketch, "E265", {"start": v(18.76, -3.25) * mm, "mid": v(18.73, -3.28) * mm, "end": v(18.71, -3.33) * mm});
            skArc(sketch, "E266", {"start": v(18.82, -3.25) * mm, "mid": v(18.79, -3.24) * mm, "end": v(18.76, -3.25) * mm});
            skArc(sketch, "E267", {"start": v(18.92, -3.3) * mm, "mid": v(18.87, -3.27) * mm, "end": v(18.82, -3.25) * mm});
            skArc(sketch, "E268", {"start": v(18.92, -3.3) * mm, "mid": v(19.2, -3.42) * mm, "end": v(19.48, -3.52) * mm});
            skArc(sketch, "E269", {"start": v(19.48, -3.52) * mm, "mid": v(19.7, -3.6) * mm, "end": v(19.93, -3.65) * mm});
            skArc(sketch, "E270", {"start": v(19.93, -3.65) * mm, "mid": v(20.16, -3.67) * mm, "end": v(20.4, -3.66) * mm});
            skArc(sketch, "E271", {"start": v(20.4, -3.66) * mm, "mid": v(20.94, -3.6) * mm, "end": v(21.47, -3.5) * mm});
            skArc(sketch, "E272", {"start": v(21.47, -3.5) * mm, "mid": v(21.71, -3.45) * mm, "end": v(21.96, -3.39) * mm});
            skArc(sketch, "E273", {"start": v(21.96, -3.39) * mm, "mid": v(22.03, -3.37) * mm, "end": v(22.1, -3.34) * mm});
            skArc(sketch, "E274", {"start": v(22.1, -3.34) * mm, "mid": v(22.13, -3.33) * mm, "end": v(22.16, -3.3) * mm});
            skLineSegment(sketch, "E275", {"start": v(13.71, 5.8) * mm, "end": v(13.49, 5.6) * mm});
            skArc(sketch, "E276", {"start": v(13.49, 5.6) * mm, "mid": v(13.3, 5.4) * mm, "end": v(13.13, 5.2) * mm});
            skArc(sketch, "E277", {"start": v(13.13, 5.2) * mm, "mid": v(13.08, 5.1) * mm, "end": v(13.05, 5.01) * mm});
            skArc(sketch, "E278", {"start": v(13.05, 5.01) * mm, "mid": v(13.03, 4.93) * mm, "end": v(13.03, 4.84) * mm});
            skArc(sketch, "E279", {"start": v(13.03, 4.84) * mm, "mid": v(13.06, 4.69) * mm, "end": v(13.11, 4.54) * mm});
            skArc(sketch, "E280", {"start": v(13.11, 4.54) * mm, "mid": v(13.2, 4.33) * mm, "end": v(13.3, 4.12) * mm});
            skArc(sketch, "E281", {"start": v(13.3, 4.12) * mm, "mid": v(13.32, 4.07) * mm, "end": v(13.35, 4.02) * mm});
            skArc(sketch, "E282", {"start": v(13.35, 4.02) * mm, "mid": v(13.37, 3.98) * mm, "end": v(13.4, 3.95) * mm});
            skArc(sketch, "E283", {"start": v(13.4, 3.95) * mm, "mid": v(13.42, 3.93) * mm, "end": v(13.45, 3.94) * mm});
            skArc(sketch, "E284", {"start": v(13.45, 3.94) * mm, "mid": v(13.54, 3.97) * mm, "end": v(13.63, 4.01) * mm});
            skArc(sketch, "E285", {"start": v(13.63, 4.01) * mm, "mid": v(13.7, 4.05) * mm, "end": v(13.76, 4.1) * mm});
            skArc(sketch, "E286", {"start": v(13.76, 4.1) * mm, "mid": v(13.82, 4.2) * mm, "end": v(13.85, 4.3) * mm});
            skArc(sketch, "E287", {"start": v(13.85, 4.3) * mm, "mid": v(13.85, 4.5) * mm, "end": v(13.84, 4.7) * mm});
            skArc(sketch, "E288", {"start": v(13.83, 5.02) * mm, "mid": v(13.83, 4.86) * mm, "end": v(13.84, 4.7) * mm});
            skArc(sketch, "E289", {"start": v(13.9, 5.29) * mm, "mid": v(13.85, 5.16) * mm, "end": v(13.83, 5.02) * mm});
            skLineSegment(sketch, "E290", {"start": v(13.9, 5.29) * mm, "end": v(13.98, 5.53) * mm});
            skLineSegment(sketch, "E291", {"start": v(13.98, 5.53) * mm, "end": v(13.71, 5.8) * mm});
            skArc(sketch, "E292", {"start": v(12.7, 6) * mm, "mid": v(12.77, 6.1) * mm, "end": v(12.79, 6.24) * mm});
            skArc(sketch, "E293", {"start": v(12.79, 6.24) * mm, "mid": v(12.76, 6.4) * mm, "end": v(12.69, 6.55) * mm});
            skArc(sketch, "E294", {"start": v(12.69, 6.55) * mm, "mid": v(12.61, 6.67) * mm, "end": v(12.52, 6.76) * mm});
            skArc(sketch, "E295", {"start": v(12.52, 6.76) * mm, "mid": v(12.5, 6.78) * mm, "end": v(12.47, 6.77) * mm});
            skArc(sketch, "E296", {"start": v(12.47, 6.77) * mm, "mid": v(12.46, 6.75) * mm, "end": v(12.46, 6.72) * mm});
            skArc(sketch, "E297", {"start": v(12.33, 6.4) * mm, "mid": v(12.4, 6.55) * mm, "end": v(12.46, 6.72) * mm});
            skLineSegment(sketch, "E298", {"start": v(12.33, 6.4) * mm, "end": v(12.21, 6.13) * mm});
            skLineSegment(sketch, "E299", {"start": v(12.21, 6.13) * mm, "end": v(12.4, 6.03) * mm});
            skArc(sketch, "E300", {"start": v(12.4, 6.03) * mm, "mid": v(12.5, 5.98) * mm, "end": v(12.6, 5.94) * mm});
            skArc(sketch, "E301", {"start": v(12.6, 5.94) * mm, "mid": v(12.63, 5.94) * mm, "end": v(12.65, 5.95) * mm});
            skArc(sketch, "E302", {"start": v(12.65, 5.95) * mm, "mid": v(12.68, 5.97) * mm, "end": v(12.7, 6) * mm});
            skLineSegment(sketch, "E303", {"start": v(-25, -15) * mm, "end": v(25, -15) * mm});
            skLineSegment(sketch, "E304", {"start": v(25, -15) * mm, "end": v(25, 15) * mm});
            skLineSegment(sketch, "E305", {"start": v(25, 15) * mm, "end": v(-25, 15) * mm});
            skLineSegment(sketch, "E306", {"start": v(-25, 15) * mm, "end": v(-25, -15) * mm});
            skSolve(sketch);
        }
        {
            var Q0;
            Q0=makeQuery(id+"F2.imprint","IMPRINT",FACE,{"disambiguationData":[TD([[makeQuery(id+"F2.imprint","IMPRINT",EDGE,{"derivedFrom":sQuery(id+"F2.wireOp",EDGE,"E1")}),1.0]])]});
            extrude(context, id + "F3", {"entities" : qUnion([Q0]), "operationType" : NewBodyOperationType.ADD, "oppositeDirection" : true, "depth" : 7 * mm});
        }
        {
            var Q0;
            Q0=makeQuery(id+"F1.opExtrude","CAP_FACE",FACE,{"disambiguationData":[OSD([sQuery(id+"F0.wireOp",EDGE,"E0.bottom"),sQuery(id+"F0.wireOp",EDGE,"E0.top"),sQuery(id+"F0.wireOp",EDGE,"E0.left"),sQuery(id+"F0.wireOp",EDGE,"E0.right")])],"isStart":false});
            var sketch = newSketch(context, id + "F4", { "sketchPlane" : qUnion([Q0])});
            skText(sketch, "E307", { "text": "Sabine", "fontName": "OpenSans-Bold.ttf"});
            skText(sketch, "E308", { "text": "Dirk", "fontName": "OpenSans-Bold.ttf"});
            const initialGuessF4  = {"E307": [-0.019, 0.00163, 1, 0, 0.006], "E308": [-0.0182, -0.00828, 1, 0, 0.006]};
            skSetInitialGuess(sketch, initialGuessF4);
            skSolve(sketch);
        }
        {
            var Q0;
            Q0 = qSketchRegion(id + "F4", true);
            extrude(context, id + "F5", {"entities" : qUnion([Q0]), "operationType" : NewBodyOperationType.ADD, "oppositeDirection" : true, "depth" : 7 * mm});
        }
    });
